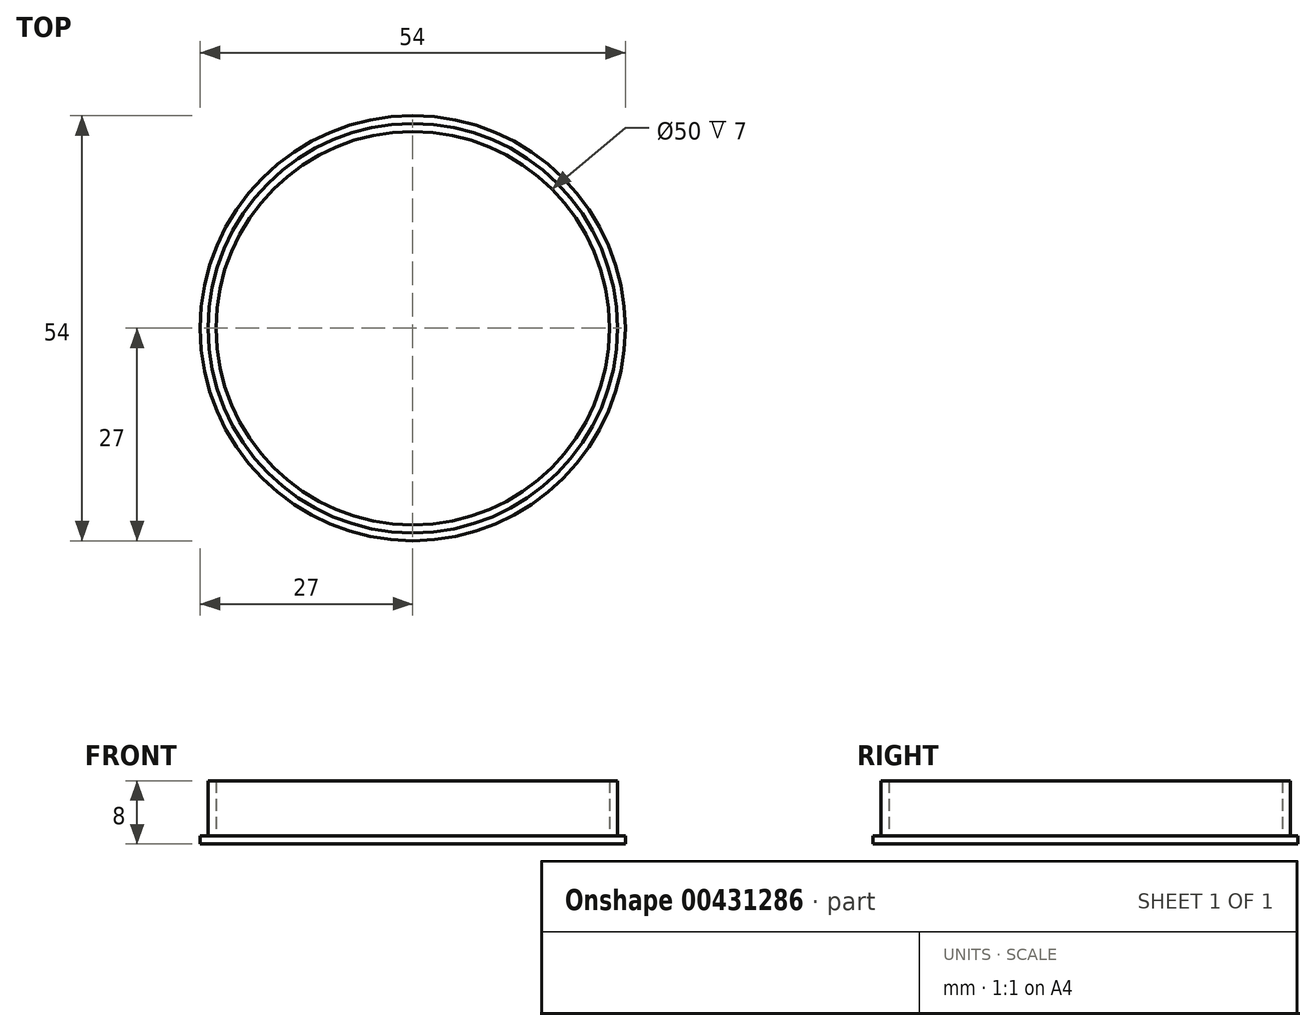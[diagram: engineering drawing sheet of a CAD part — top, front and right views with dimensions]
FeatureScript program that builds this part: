
annotation { "Feature Type Name" : "Feature", "Feature Type Description" : "" }
export const myFeature = defineFeature(function(context is Context, id is Id, definition is map)
    precondition{}
    {
        {
            var Q0;
            Q0=qCreatedBy(makeId("Top.planeOp"),FACE);
            var sketch = newSketch(context, id + "F0", { "sketchPlane" : qUnion([Q0])});
            skCircle(sketch, "E0", {"center": v(0, 0) * mm, "radius": 26 * mm});
            skCircle(sketch, "E1", {"center": v(0, 0) * mm, "radius": 27 * mm});
            skCircle(sketch, "E2", {"center": v(0, 0) * mm, "radius": 25 * mm});
            skSolve(sketch);
        }
        {
            var Q0;
            Q0 = qSketchRegion(id + "F0", true);
            var Q1;
            Q1=makeQuery(id+"F0.imprint","IMPRINT",FACE,{"disambiguationData":[TD([[makeQuery(id+"F0.imprint","IMPRINT",EDGE,{"derivedFrom":sQuery(id+"F0.wireOp",EDGE,"E2")}),1.0]])]});
            var Q2;
            Q2=makeQuery(id+"F0.imprint","IMPRINT",FACE,{"disambiguationData":[TD([[makeQuery(id+"F0.imprint","IMPRINT",EDGE,{"derivedFrom":sQuery(id+"F0.wireOp",EDGE,"E0")}),1.0]])]});
            extrude(context, id + "F1", {"entities" : qUnion([Q0, Q1, Q2]), "depth" : 1 * mm});
        }
        {
            var Q0;
            Q0=makeQuery(id+"F0.imprint","IMPRINT",FACE,{"disambiguationData":[TD([[makeQuery(id+"F0.imprint","IMPRINT",EDGE,{"derivedFrom":sQuery(id+"F0.wireOp",EDGE,"E0")}),1.0]])]});
            extrude(context, id + "F2", {"entities" : qUnion([Q0]), "operationType" : NewBodyOperationType.ADD, "depth" : 8 * mm});
        }
    });
